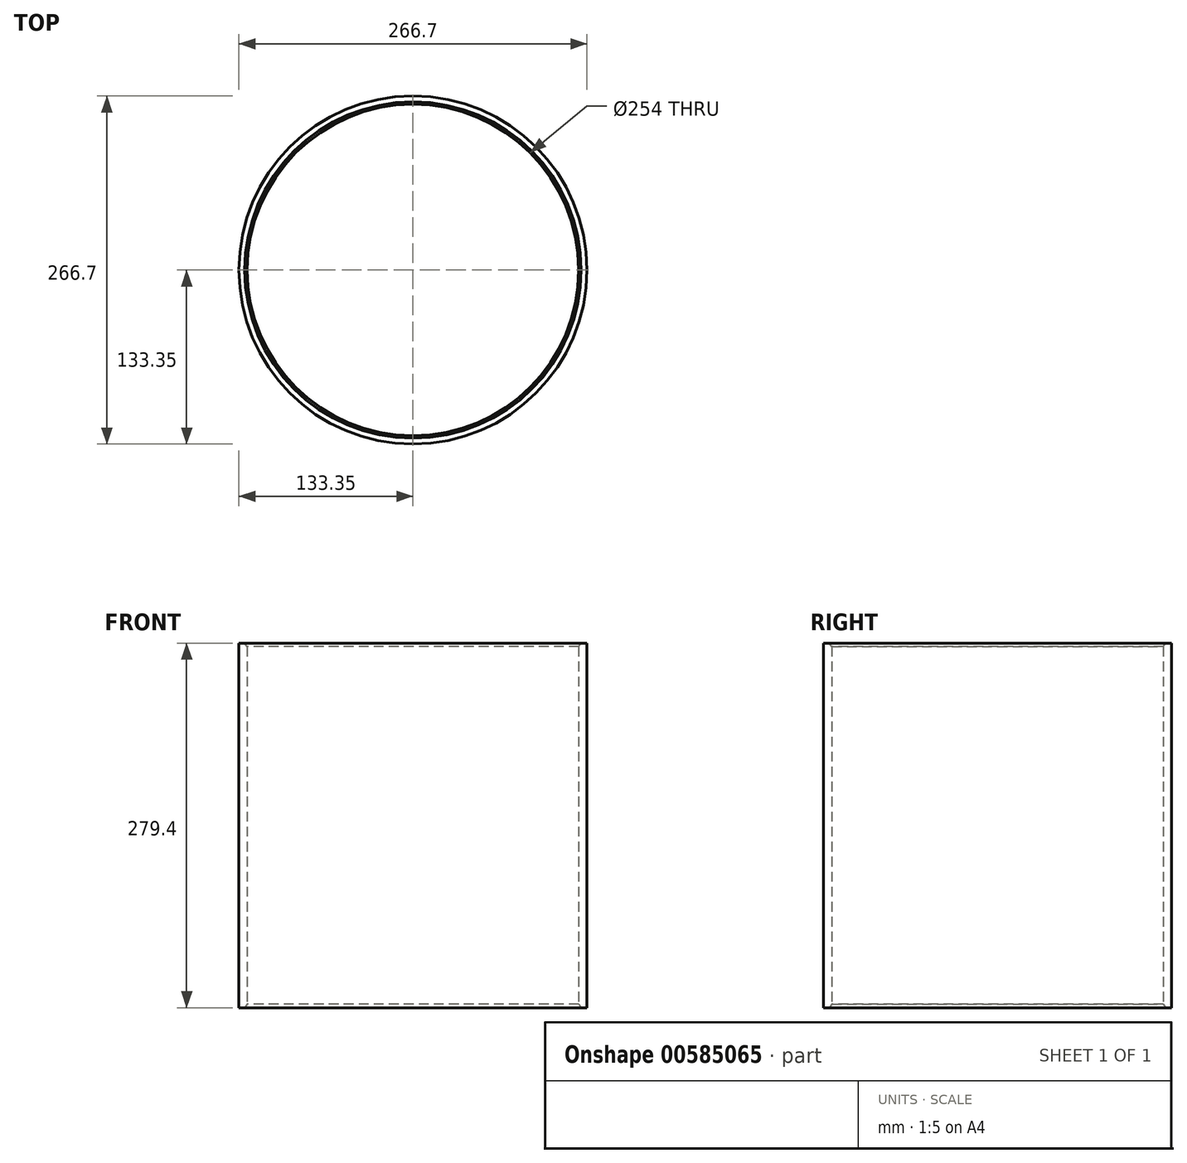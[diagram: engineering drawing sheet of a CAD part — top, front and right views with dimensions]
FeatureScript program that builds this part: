
annotation { "Feature Type Name" : "Feature", "Feature Type Description" : "" }
export const myFeature = defineFeature(function(context is Context, id is Id, definition is map)
    precondition{}
    {
        {
            var Q0;
            Q0=qCreatedBy(makeId("Top.planeOp"),FACE);
            var sketch = newSketch(context, id + "F0", { "sketchPlane" : qUnion([Q0])});
            skCircle(sketch, "E0", {"center": v(0, 0) * mm, "radius": 133.35 * mm});
            skCircle(sketch, "E1", {"center": v(0, 0) * mm, "radius": 127 * mm});
            skSolve(sketch);
        }
        {
            var Q0;
            Q0 = qSketchRegion(id + "F0", true);
            extrude(context, id + "F1", {"entities" : qUnion([Q0]), "depth" : 279.4 * mm, "offsetDistance" : 25.4 * mm});
        }
        {
            var Q0;
            Q0=makeQuery(id+"F1.opExtrude","CAP_FACE",FACE,{"disambiguationData":[OSD([sQuery(id+"F0.wireOp",EDGE,"E0"),sQuery(id+"F0.wireOp",EDGE,"E1")])],"isStart":false});
            var sketch = newSketch(context, id + "F2", { "sketchPlane" : qUnion([Q0])});
            skCircle(sketch, "E2", {"center": v(0, 0) * mm, "radius": 130.18 * mm});
            skSolve(sketch);
        }
        {
            var Q0;
            Q0=makeQuery(id+"F1.opExtrude","CAP_FACE",FACE,{"disambiguationData":[OSD([sQuery(id+"F0.wireOp",EDGE,"E0"),sQuery(id+"F0.wireOp",EDGE,"E1")])],"isStart":true});
            var sketch = newSketch(context, id + "F3", { "sketchPlane" : qUnion([Q0])});
            skCircle(sketch, "E3", {"center": v(0, 0) * mm, "radius": 133.35 * mm});
            skCircle(sketch, "E4", {"center": v(0, 0) * mm, "radius": 130.18 * mm});
            skSolve(sketch);
        }
        {
            var Q0;
            Q0=qCreatedBy(makeId("Right.planeOp"),FACE);
            var sketch = newSketch(context, id + "F4", { "sketchPlane" : qUnion([Q0])});
            skLineSegment(sketch, "E5", {"start": v(0, 0) * mm, "end": v(0, 15.88) * mm, "construction": true});
            skLineSegment(sketch, "E6", {"start": v(0, 15.88) * mm, "end": v(0, 60.33) * mm, "construction": true});
            skLineSegment(sketch, "E7", {"start": v(0, 60.33) * mm, "end": v(0, 269.88) * mm, "construction": true});
            skLineSegment(sketch, "E8", {"start": v(0, 269.88) * mm, "end": v(0, 314.33) * mm, "construction": true});
            skCircle(sketch, "E9", {"center": v(0, 38.1) * mm, "radius": 22.23 * mm});
            skCircle(sketch, "E10", {"center": v(0, 292.1) * mm, "radius": 22.23 * mm});
            skSolve(sketch);
        }
        {
            var Q0;
            Q0=makeQuery(id+"F1.opExtrude","CAP_EDGE",EDGE,{"disambiguationData":[OSD([sQuery(id+"F0.wireOp",EDGE,"E1")])],"isStart":false});
            var Q1;
            Q1=makeQuery(id+"F1.opExtrude","CAP_EDGE",EDGE,{"disambiguationData":[OSD([sQuery(id+"F0.wireOp",EDGE,"E1")])],"isStart":true});
            chamfer(context, id + "F5", {"entities" : qUnion([Q0, Q1]), "chamferType" : ChamferType.OFFSET_ANGLE, "width" : 1.9 * mm, "oppositeDirection" : true, "angle" : 55 * degree, "tangentPropagation" : true});
        }
    });
